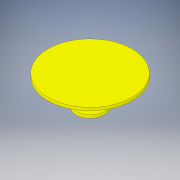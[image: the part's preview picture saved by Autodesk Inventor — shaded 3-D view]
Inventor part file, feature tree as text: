
AUTODESK INVENTOR PART (.ipt)
format: ipt  version: 2019 (Build 230136000, 136)  size: 126,976 bytes
history: native  units: mm
features: extrude x4, sketch x4
ambient origin geometry x8: Origin, YZ Plane, XZ Plane, XY Plane, X Axis, Y Axis, Z Axis, Center Point
bodies: Solid1 (feature_tree)
feature tree (8):
  extrude  "Extrusion1"  Depth=25.0mm TaperAngle=0.0deg
  extrude  "Extrusion2"  Depth=3.18mm TaperAngle=0.0deg
  extrude  "Extrusion3"  Depth=3.18mm TaperAngle=0.0deg
  extrude  "Extrusion4"  Depth=3.18mm TaperAngle=0.0deg
  sketch  "Sketch1"  dims[d0=10.0mm d1=25.0mm d2=0.0mm]
  sketch  "Sketch2"  dims[d3=90.0mm d4=3.18mm d5=0.0mm]
  sketch  "Sketch3"  dims[d6=30.0mm d7=3.18mm d8=0.0mm]
  sketch  "Sketch4"  dims[d9=12.0mm d10=3.18mm d11=0.0mm]
